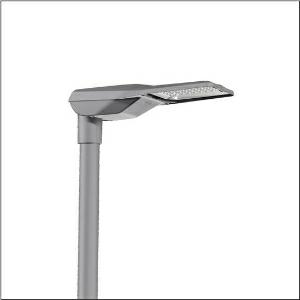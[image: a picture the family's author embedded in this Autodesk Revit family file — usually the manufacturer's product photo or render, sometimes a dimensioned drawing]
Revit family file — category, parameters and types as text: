
# Revit family: streetlight_sl_21_iq_mini___pl52_5xe2h31g08hb_1606
name_source: partatom
category: Lighting Fixtures
units: mm (PartAtom-declared; Revit-internal decimal feet)

## family parameters
Cut with Voids When Loaded = No
Host = Face
Light Source = No
Part Type = Normal
Room Calculation Point = No
Round Connector Dimension = Use Diameter
Shared = No

## types (1)
- --- (1 x LED, 9290 lm, 70.9 W, 3000K)
    Apparent Load = 71 VA
    CIE Flux Codes = 27 59 98 100 100
    Color Rendering = 70
    Color Temperature = 3000K
    Default Elevation = 1800 mm
    Description = Streetlight SL 21 mini, mast luminaire, primary light control with lens, of PMMA, primary optical cover: cover, of toughened safety glass, transparent, light distribution: PL52, light emission: direct distribution, primary light characteristic: asymmetric, installation type: post-top, side-entry, LED, High Power LED, rated luminous flux: 9.290lm, luminous efficacy: 131lm/W, light colour: 730, colour temperature: 3000K, control gear: ECG iQ, control: Street-Remote, Auto-Match, Temp-Guard, Lumen-Switch, Night-Set, Smart-Wire, Light-Fading, Desk-Remote (wireless, voltage-free reading and setting of iQ features in the workshop via application-optimized NFC function/RFID function), optimised constant luminous flux control (CLO 2.0), mains connection: 220..240V, AC, 50/60Hz, start of lifetime: 71W, end of lifetime: 75W, reduction: 31W, luminaire housing, of diecast aluminium, powder-coated, Siteco® metallic grey (DB 702S), corrosivity category C5 according to DIN EN ISO 12944, length: 628mm, width: 235mm, height: 110mm, spigot size: 60/76mm (post-top) and 42/60/76mm (side-entry), mast flange for spigot size: 42mm: 5XC10008XM4, 60mm: 5XC10008XM2, 76/60mm: 5XC10108XM1, protection rating (complete): IP66, insulation class (complete): insulation class II (safety insulation), certification: CE, ENEC, VDE, impact resistance: IK09, permissible operating ambient temperature for outdoor applications: -40..+50°C, standard-compliant lighting for roads and squares, packaging unit: 1 piece

Light Distribution: PL52
    Height = 110 mm
    Lamp = 1 x LED
    Lamp Light Flux = 9290 lm
    Lamp Power = 70.9 W
    Lamp count = 1
    Length = 625 mm
    Luminous efficacy = 131 lm/W
    Manufacturer = Siteco
    ModVariant = No
    Model = 5XE2H31G08HB
    Number of Poles = 1
    OnlyDefault = Yes
    Power Factor = 1
    Product Name = Streetlight SL 21 iQ mini | PL52
    Product group = mast luminaire | pylon top
    ProductGroupID = 6100
    Protection Class = Protection class II
    Protection Degree = IP 66
    RLX_Detail_Level = 1
    RlxData = <blob elided: 101889 chars, md5=5a1c6a2f>
    Socket = socket
    Standby Power = 0 W
    System Light Flux = 9290 lm
    System Power = 71 W
    Type Comments = factory setting: luminous flux: 100 % | dim-lin: 254 | 711 mA
    Type Image = l_1003519.jpg
    URL = http://relux.com
    VarID = @adj_069683
    Voltage = 0 V
    Weight = 0.00 kg
    Width = 234 mm

## geometry (parser evidence)
native form markers: Blend x4, Sweep x11
no freeform markers — native parametric forms only
